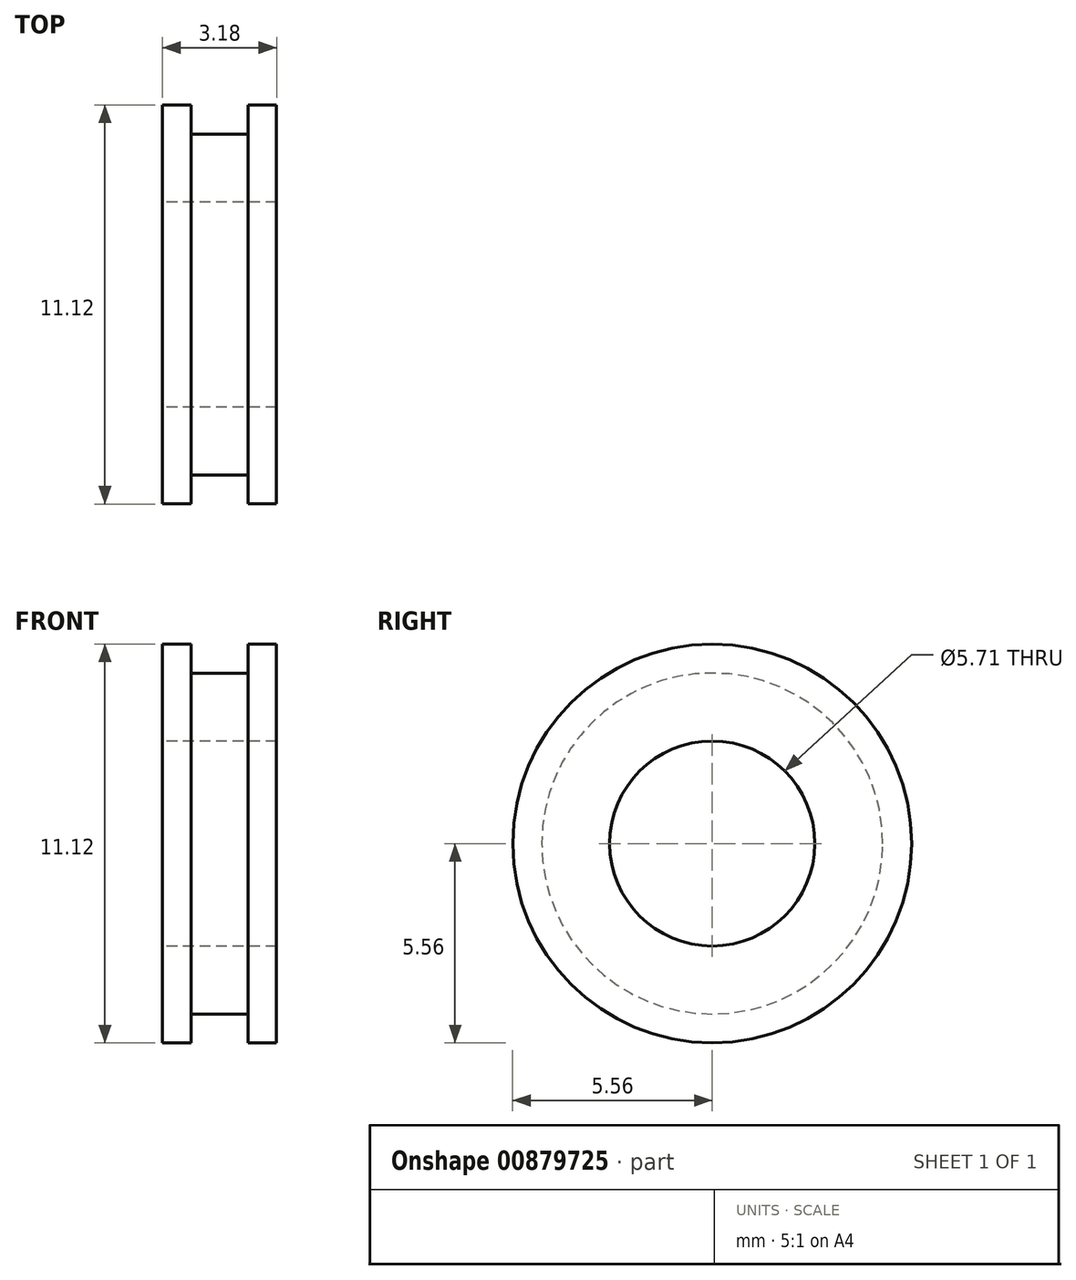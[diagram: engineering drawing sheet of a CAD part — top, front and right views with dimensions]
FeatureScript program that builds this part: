
annotation { "Feature Type Name" : "Feature", "Feature Type Description" : "" }
export const myFeature = defineFeature(function(context is Context, id is Id, definition is map)
    precondition{}
    {
        {
            var Q0;
            Q0=qCreatedBy(makeId("Right.planeOp"),FACE);
            var sketch = newSketch(context, id + "F0", { "sketchPlane" : qUnion([Q0])});
            skCircle(sketch, "E0", {"center": v(0, 0) * mm, "radius": 5.56 * mm});
            skCircle(sketch, "E1", {"center": v(0, 0) * mm, "radius": 2.86 * mm});
            skSolve(sketch);
        }
        {
            var Q0;
            Q0 = qSketchRegion(id + "F0", true);
            extrude(context, id + "F1", {"entities" : qUnion([Q0]), "depth" : 3.17 * mm, "offsetDistance" : 25.4 * mm});
        }
        {
            var Q0;
            Q0=qCreatedBy(makeId("Front.planeOp"),FACE);
            var sketch = newSketch(context, id + "F2", { "sketchPlane" : qUnion([Q0])});
            skLineSegment(sketch, "E2.bottom", {"start": v(0.8, 4.75) * mm, "end": v(2.38, 4.75) * mm});
            skLineSegment(sketch, "E2.top", {"start": v(0.8, 5.56) * mm, "end": v(2.38, 5.56) * mm});
            skLineSegment(sketch, "E2.left", {"start": v(0.8, 4.75) * mm, "end": v(0.8, 5.56) * mm});
            skLineSegment(sketch, "E2.right", {"start": v(2.38, 4.75) * mm, "end": v(2.38, 5.56) * mm});
            skLineSegment(sketch, "E3", {"start": v(0, 0) * mm, "end": v(-6.9, 0) * mm, "construction": true});
            skSolve(sketch);
        }
        {
            var Q0;
            Q0 = qSketchRegion(id + "F2", true);
            var Q1;
            Q1=sQuery(id+"F2.wireOp",EDGE,"E3");
            revolve(context, id + "F3", {"operationType" : NewBodyOperationType.REMOVE, "surfaceOperationType" : NewSurfaceOperationType.NEW, "entities" : qUnion([Q0]), "axis" : qUnion([Q1]), "revolveType" : RevolveType.FULL, "oppositeDirection" : true});
        }
    });
